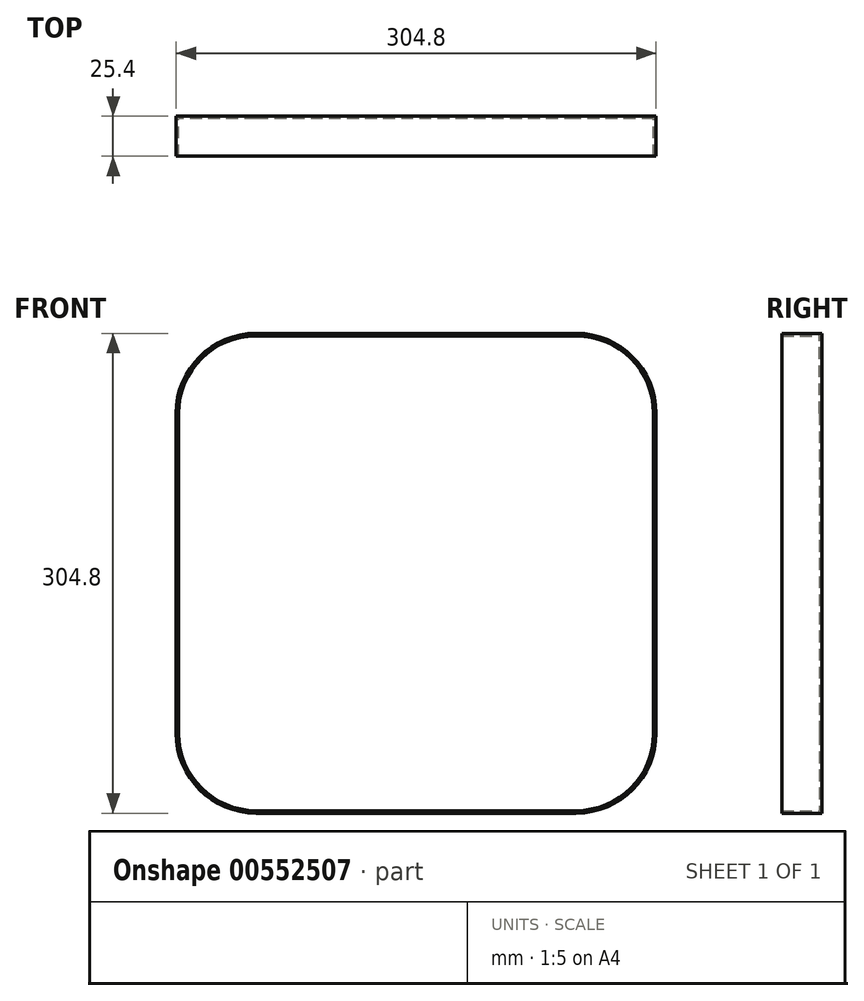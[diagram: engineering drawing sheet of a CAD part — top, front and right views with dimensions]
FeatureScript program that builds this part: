
annotation { "Feature Type Name" : "Feature", "Feature Type Description" : "" }
export const myFeature = defineFeature(function(context is Context, id is Id, definition is map)
    precondition{}
    {
        {
            var Q0;
            Q0=qCreatedBy(makeId("Front.planeOp"),FACE);
            var sketch = newSketch(context, id + "F0", { "sketchPlane" : qUnion([Q0])});
            skLineSegment(sketch, "E0.bottom", {"start": v(101.6, 152.4) * mm, "end": v(-101.6, 152.4) * mm});
            skLineSegment(sketch, "E0.top", {"start": v(101.6, -152.4) * mm, "end": v(-101.6, -152.4) * mm});
            skLineSegment(sketch, "E0.left", {"start": v(152.4, 101.6) * mm, "end": v(152.4, -101.6) * mm});
            skLineSegment(sketch, "E0.right", {"start": v(-152.4, 101.6) * mm, "end": v(-152.4, -101.6) * mm});
            skPoint(sketch, "E0.middle", {"position": v(0, 0) * mm});
            skPoint(sketch, "E1.visualSharp", {"position": v(152.4, 152.4) * mm});
            skArc(sketch, "E1.filletArc", {"start": v(152.4, 101.6) * mm, "mid": v(137.52, 137.52) * mm, "end": v(101.6, 152.4) * mm});
            skPoint(sketch, "E2.visualSharp", {"position": v(-152.4, 152.4) * mm});
            skArc(sketch, "E2.filletArc", {"start": v(-101.6, 152.4) * mm, "mid": v(-137.52, 137.52) * mm, "end": v(-152.4, 101.6) * mm});
            skPoint(sketch, "E3.visualSharp", {"position": v(152.4, -152.4) * mm});
            skArc(sketch, "E3.filletArc", {"start": v(101.6, -152.4) * mm, "mid": v(137.52, -137.52) * mm, "end": v(152.4, -101.6) * mm});
            skPoint(sketch, "E4.visualSharp", {"position": v(-152.4, -152.4) * mm});
            skArc(sketch, "E4.filletArc", {"start": v(-152.4, -101.6) * mm, "mid": v(-137.52, -137.52) * mm, "end": v(-101.6, -152.4) * mm});
            skSolve(sketch);
        }
        {
            var Q0;
            Q0=makeQuery(id+"F0.imprint","IMPRINT",FACE,{"disambiguationData":[TD([[makeQuery(id+"F0.imprint","IMPRINT",EDGE,{"derivedFrom":sQuery(id+"F0.wireOp",EDGE,"E0.bottom")}),1.0]])]});
            extrude(context, id + "F1", {"entities" : qUnion([Q0]), "depth" : 25.4 * mm, "offsetDistance" : 25.4 * mm});
        }
        {
            var Q0;
            Q0=makeQuery(id+"F1.opExtrude","CAP_FACE",FACE,{"disambiguationData":[OSD([sQuery(id+"F0.wireOp",EDGE,"E0.bottom"),sQuery(id+"F0.wireOp",EDGE,"E0.top"),sQuery(id+"F0.wireOp",EDGE,"E0.left"),sQuery(id+"F0.wireOp",EDGE,"E0.right"),sQuery(id+"F0.wireOp",EDGE,"E1.filletArc"),sQuery(id+"F0.wireOp",EDGE,"E2.filletArc"),sQuery(id+"F0.wireOp",EDGE,"E3.filletArc"),sQuery(id+"F0.wireOp",EDGE,"E4.filletArc")])],"isStart":false});
            shell(context, id + "F2", {"entities" : qUnion([Q0]), "thickness" : 1.6 * mm});
        }
    });
